# Revit family: TCAT24-CM
name_source: partatom
category: Lighting Fixtures
revit_build: Autodesk Revit Architecture 2012 (Build: 20110309_2315(x64)
units: mm (PartAtom-declared; Revit-internal decimal feet)

## types (2) — shared parameters
Apparent Load = 0 VA
Backbox = Hubbell - White
Certifications = UL1598,2108 & CSA
Color Filter = 16777215
Default Elevation = 48 "
Description = LED Twin Contempory Architectural Troffer.
Dimming Lamp Color Temperature Shift = <None>
Emit Shape Visible in Rendering = No
Emit from Rectangle Width = 4 "
Lamp = LED Lamp
Light Bulb = Hubbell - White Glass
Load Classification = Lighting
Manufacturer = Columbia Lighting
Manufacturer Fax = (866)-898-1065
Suspension Height = 48 "
Tilt Angle = -90.00°
URL = http://www.columbialighting.com
Voltage = 120 V
Warranty = Five year warranty

## per-type parameters (varying)
| type | Emit from Rectangle Length | Photometric Web File | Row Length | Wattage Comments | Watts | zz Length |
| TCAT24 | 47 " | TCAT24-30HLx-EDU.ies | 48 " | 19-69 W | 69 W | 47 " |
| TCAT22 | 23 " | TCAT22-30HLx-EDU.ies | 24 " | 12-37 W | 37 W | 23 " |

note: column(s) folded — value = type name in every type: Model

## geometry (parser evidence)
native form markers: Sweep x5
no freeform markers — native parametric forms only
